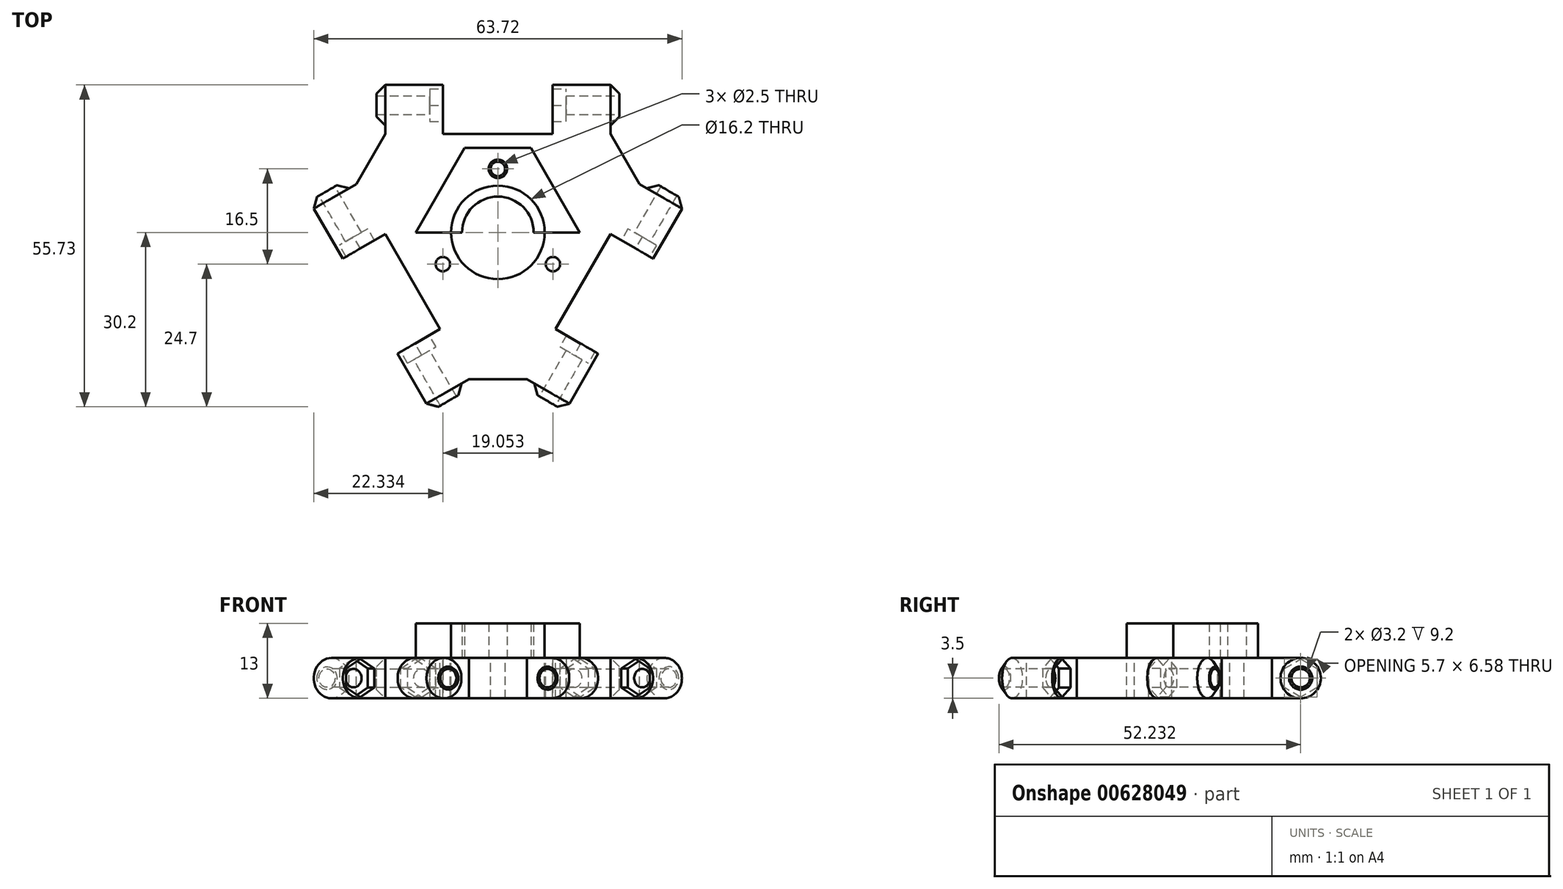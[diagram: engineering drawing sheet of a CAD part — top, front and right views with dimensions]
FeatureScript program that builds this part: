
annotation { "Feature Type Name" : "Feature", "Feature Type Description" : "" }
export const myFeature = defineFeature(function(context is Context, id is Id, definition is map)
    precondition{}
    {
        {
            assignVariable(context, id + "F0", {"name" : "side_inner_gap_width", "anyValue" : 19 * mm});
        }
        {
            assignVariable(context, id + "F1", {"name" : "side_arm_width", "anyValue" : 10 * mm});
        }
        {
            assignVariable(context, id + "F2", {"name" : "baseplate_thickness", "anyValue" : 7 * mm});
        }
        {
            assignVariable(context, id + "F3", {"name" : "rod_holder_indent", "anyValue" : 1.5 * mm});
        }
        {
            assignVariable(context, id + "F4", {"name" : "M3_nut_height", "anyValue" : 2.3 * mm});
        }
        {
            var Q0;
            Q0=qCreatedBy(makeId("Top.planeOp"),FACE);
            var sketch = newSketch(context, id + "F5", { "sketchPlane" : qUnion([Q0])});
            skCircle(sketch, "E0", {"center": v(0, 0) * mm, "radius": 8.1 * mm});
            skLineSegment(sketch, "E1", {"start": v(-9.5, 17.03) * mm, "end": v(9.5, 17.03) * mm});
            skLineSegment(sketch, "E2", {"start": v(9.5, 17.03) * mm, "end": v(9.5, 25.53) * mm});
            skLineSegment(sketch, "E3", {"start": v(9.5, 25.53) * mm, "end": v(19.5, 25.53) * mm});
            skLineSegment(sketch, "E4", {"start": v(19.5, 25.53) * mm, "end": v(19.5, 17.03) * mm});
            skLineSegment(sketch, "E5", {"start": v(19.5, 17.03) * mm, "end": v(24.5, 8.37) * mm});
            skLineSegment(sketch, "E6", {"start": v(24.5, 8.37) * mm, "end": v(31.86, 4.12) * mm});
            skLineSegment(sketch, "E7", {"start": v(31.86, 4.12) * mm, "end": v(26.86, -4.54) * mm});
            skLineSegment(sketch, "E8", {"start": v(-19.5, 17.03) * mm, "end": v(-19.5, 25.53) * mm});
            skLineSegment(sketch, "E9", {"start": v(-19.5, 25.53) * mm, "end": v(-9.5, 25.53) * mm});
            skLineSegment(sketch, "E10", {"start": v(-9.5, 25.53) * mm, "end": v(-9.5, 17.03) * mm});
            skLineSegment(sketch, "E11", {"start": v(26.86, -4.54) * mm, "end": v(19.5, -0.29) * mm});
            skLineSegment(sketch, "E12", {"start": v(19.5, -0.29) * mm, "end": v(10, -16.74) * mm});
            skLineSegment(sketch, "E13", {"start": v(10, -16.74) * mm, "end": v(17.36, -21) * mm});
            skLineSegment(sketch, "E14", {"start": v(17.36, -21) * mm, "end": v(12.36, -29.65) * mm});
            skLineSegment(sketch, "E15", {"start": v(12.36, -29.65) * mm, "end": v(5, -25.4) * mm});
            skLineSegment(sketch, "E16", {"start": v(5, -25.4) * mm, "end": v(-5, -25.4) * mm});
            skLineSegment(sketch, "E17", {"start": v(-5, -25.4) * mm, "end": v(-12.36, -29.65) * mm});
            skLineSegment(sketch, "E18", {"start": v(-12.36, -29.65) * mm, "end": v(-17.36, -21) * mm});
            skLineSegment(sketch, "E19", {"start": v(-17.36, -21) * mm, "end": v(-10, -16.74) * mm});
            skLineSegment(sketch, "E20", {"start": v(-19.5, 17.03) * mm, "end": v(-24.5, 8.37) * mm});
            skLineSegment(sketch, "E21", {"start": v(-24.5, 8.37) * mm, "end": v(-31.86, 4.12) * mm});
            skLineSegment(sketch, "E22", {"start": v(-31.86, 4.12) * mm, "end": v(-26.86, -4.54) * mm});
            skLineSegment(sketch, "E23", {"start": v(-26.86, -4.54) * mm, "end": v(-19.5, -0.29) * mm});
            skLineSegment(sketch, "E24", {"start": v(-19.5, -0.29) * mm, "end": v(-10, -16.74) * mm});
            skLineSegment(sketch, "E25", {"start": v(-9.5, 17.03) * mm, "end": v(0, 0) * mm, "construction": true});
            skLineSegment(sketch, "E26", {"start": v(19.5, -0.29) * mm, "end": v(0, 0) * mm, "construction": true});
            skLineSegment(sketch, "E27", {"start": v(-10, -16.74) * mm, "end": v(0, 0) * mm, "construction": true});
            skArc(sketch, "E28", {"start": v(-6.2, 0) * mm, "mid": v(0, 6.2) * mm, "end": v(6.2, 0) * mm});
            skLineSegment(sketch, "E29", {"start": v(6.2, 0) * mm, "end": v(14.2, 0) * mm});
            skLineSegment(sketch, "E30", {"start": v(14.2, 0) * mm, "end": v(5.75, 14.64) * mm});
            skLineSegment(sketch, "E31", {"start": v(5.75, 14.64) * mm, "end": v(-5.75, 14.64) * mm});
            skLineSegment(sketch, "E32", {"start": v(-5.75, 14.64) * mm, "end": v(-14.2, 0) * mm});
            skLineSegment(sketch, "E33", {"start": v(-14.2, 0) * mm, "end": v(-6.2, 0) * mm});
            skCircle(sketch, "E34", {"center": v(0, 11) * mm, "radius": 1.6 * mm});
            skCircle(sketch, "E35", {"center": v(0, 11) * mm, "radius": 1.25 * mm});
            skLineSegment(sketch, "E36", {"start": v(0, 11) * mm, "end": v(0, 0) * mm, "construction": true});
            skCircle(sketch, "E37.1.0", {"center": v(-9.53, -5.5) * mm, "radius": 1.25 * mm});
            skLineSegment(sketch, "E37.1.2", {"start": v(-9.53, -5.5) * mm, "end": v(0, 0) * mm, "construction": true});
            skCircle(sketch, "E37.2.0", {"center": v(9.53, -5.5) * mm, "radius": 1.25 * mm});
            skLineSegment(sketch, "E37.2.2", {"start": v(9.53, -5.5) * mm, "end": v(0, 0) * mm, "construction": true});
            skSolve(sketch);
        }
        {
            var Q0;
            Q0=makeQuery(id+"F5.imprint","IMPRINT",FACE,{"disambiguationData":[TD([[makeQuery(id+"F5.imprint","IMPRINT",EDGE,{"derivedFrom":sQuery(id+"F5.wireOp",EDGE,"E0")}),-1.0]])]});
            var Q1;
            Q1=makeQuery(id+"F5.imprint","IMPRINT",FACE,{"disambiguationData":[TD([[makeQuery(id+"F5.imprint","IMPRINT",EDGE,{"derivedFrom":sQuery(id+"F5.wireOp",EDGE,"E1")}),-1.0]])]});
            var Q2;
            Q2=makeQuery(id+"F5.imprint","IMPRINT",FACE,{"disambiguationData":[TD([[makeQuery(id+"F5.imprint","IMPRINT",EDGE,{"derivedFrom":sQuery(id+"F5.wireOp",EDGE,"E34")}),1.0]])]});
            var Q3;
            Q3=makeQuery(id+"F5.imprint","IMPRINT",FACE,{"disambiguationData":[TD([[makeQuery(id+"F5.imprint","IMPRINT",EDGE,{"derivedFrom":sQuery(id+"F5.wireOp",EDGE,"gB12h6lw-a8Tq-MIft-bfN1-dJZgKXMW2Zgf")}),-1.0]])]});
            extrude(context, id + "F6", {"entities" : qUnion([Q0, Q1, Q2, Q3]), "oppositeDirection" : true, "depth" : getVariable(context, 'baseplate_thickness'), "offsetDistance" : 25 * mm});
        }
        {
            var Q0;
            {var subQ0=sQuery(id+"F5.wireOp",EDGE,"E30");Q0=makeQuery(id+"F5.imprint","IMPRINT",FACE,{"disambiguationData":[TD([[makeQuery(id+"F5.imprint","IMPRINT",EDGE,{"derivedFrom":subQ0}),1.0]])]});}
            var Q1;
            {var subQ5=sQuery(id+"F5.wireOp",EDGE,"E28");Q1=makeQuery(id+"F5.imprint","IMPRINT",FACE,{"disambiguationData":[TD([[makeQuery(id+"F5.imprint","IMPRINT",EDGE,{"derivedFrom":subQ5}),1.0]])]});}
            extrude(context, id + "F7", {"entities" : qUnion([Q0, Q1]), "depth" : 6 * mm, "offsetDistance" : 25 * mm});
        }
        {
            var Q0;
            Q0=makeQuery(id+"F6.opExtrude","CAP_EDGE",EDGE,{"disambiguationData":[OSD([sQuery(id+"F5.wireOp",EDGE,"E14")])],"isStart":false});
            var Q1;
            Q1=makeQuery(id+"F6.opExtrude","CAP_EDGE",EDGE,{"disambiguationData":[OSD([sQuery(id+"F5.wireOp",EDGE,"E7")])],"isStart":false});
            var Q2;
            Q2=makeQuery(id+"F6.opExtrude","CAP_EDGE",EDGE,{"disambiguationData":[OSD([sQuery(id+"F5.wireOp",EDGE,"E14")])],"isStart":true});
            var Q3;
            Q3=makeQuery(id+"F6.opExtrude","CAP_EDGE",EDGE,{"disambiguationData":[OSD([sQuery(id+"F5.wireOp",EDGE,"E7")])],"isStart":true});
            var Q4;
            Q4=makeQuery(id+"F6.opExtrude","CAP_EDGE",EDGE,{"disambiguationData":[OSD([sQuery(id+"F5.wireOp",EDGE,"E18")])],"isStart":false});
            var Q5;
            Q5=makeQuery(id+"F6.opExtrude","CAP_EDGE",EDGE,{"disambiguationData":[OSD([sQuery(id+"F5.wireOp",EDGE,"E18")])],"isStart":true});
            var Q6;
            Q6=makeQuery(id+"F6.opExtrude","CAP_EDGE",EDGE,{"disambiguationData":[OSD([sQuery(id+"F5.wireOp",EDGE,"E22")])],"isStart":true});
            var Q7;
            Q7=makeQuery(id+"F6.opExtrude","CAP_EDGE",EDGE,{"disambiguationData":[OSD([sQuery(id+"F5.wireOp",EDGE,"E22")])],"isStart":false});
            var Q8;
            Q8=makeQuery(id+"F6.opExtrude","CAP_EDGE",EDGE,{"disambiguationData":[OSD([sQuery(id+"F5.wireOp",EDGE,"E3")])],"isStart":false});
            var Q9;
            Q9=makeQuery(id+"F6.opExtrude","CAP_EDGE",EDGE,{"disambiguationData":[OSD([sQuery(id+"F5.wireOp",EDGE,"E9")])],"isStart":false});
            var Q10;
            Q10=makeQuery(id+"F6.opExtrude","CAP_EDGE",EDGE,{"disambiguationData":[OSD([sQuery(id+"F5.wireOp",EDGE,"E3")])],"isStart":true});
            var Q11;
            Q11=makeQuery(id+"F6.opExtrude","CAP_EDGE",EDGE,{"disambiguationData":[OSD([sQuery(id+"F5.wireOp",EDGE,"E9")])],"isStart":true});
            fillet(context, id + "F8", {"entities" : qUnion([Q0, Q1, Q2, Q3, Q4, Q5, Q6, Q7, Q8, Q9, Q10, Q11]), "radius" : getVariable(context, 'baseplate_thickness') / 2, "tangentPropagation" : true, "allowEdgeOverflow" : false});
        }
        {
            var Q0;
            Q0=makeQuery(id+"F6.opExtrude","SWEPT_FACE",FACE,{"disambiguationData":[OSD([sQuery(id+"F5.wireOp",EDGE,"E11")])]});
            var sketch = newSketch(context, id + "F9", { "sketchPlane" : qUnion([Q0])});
            skCircle(sketch, "E38", {"center": v(22.03, -3.5) * mm, "radius": 3.5 * mm});
            skCircle(sketch, "E39.cCircle", {"center": v(22.03, -3.5) * mm, "radius": 3.3 * mm, "construction": true});
            skLineSegment(sketch, "E39.0", {"start": v(22.03, -0.2) * mm, "end": v(24.88, -1.85) * mm});
            skLineSegment(sketch, "E39.1", {"start": v(24.88, -1.85) * mm, "end": v(24.88, -5.15) * mm});
            skLineSegment(sketch, "E39.2", {"start": v(24.88, -5.15) * mm, "end": v(22.03, -6.8) * mm});
            skLineSegment(sketch, "E39.3", {"start": v(22.03, -6.8) * mm, "end": v(19.18, -5.15) * mm});
            skLineSegment(sketch, "E39.4", {"start": v(19.18, -5.15) * mm, "end": v(19.18, -1.85) * mm});
            skLineSegment(sketch, "E39.5", {"start": v(19.18, -1.85) * mm, "end": v(22.03, -0.2) * mm});
            skCircle(sketch, "E40", {"center": v(22.03, -3.5) * mm, "radius": 1.6 * mm});
            skSolve(sketch);
        }
        {
            var Q0;
            {var subQ0=sQuery(id+"F9.wireOp",EDGE,"E38");var subQ1=sQuery(id+"F5.wireOp",EDGE,"E11");var subQ4=makeQuery(id+"F9.imprint","INTERSECT",VERTEX,{"derivedFrom":[makeQuery(id+"F6.opExtrude","CAP_EDGE",EDGE,{"disambiguationData":[OSD([subQ1])],"isStart":true}),subQ0]});Q0=makeQuery(id+"F9.imprint","IMPRINT",FACE,{"disambiguationData":[TD([[makeQuery(id+"F9.imprint","IMPRINT",EDGE,{"disambiguationData":[TD([[subQ4,-1.0]])],"derivedFrom":subQ0}),1.0]])]});}
            var Q1;
            Q1=makeQuery(id+"F9.imprint","IMPRINT",FACE,{"disambiguationData":[TD([[makeQuery(id+"F9.imprint","IMPRINT",EDGE,{"derivedFrom":sQuery(id+"F9.wireOp",EDGE,"E39.0")}),-1.0]])]});
            extrude(context, id + "F10", {"entities" : qUnion([Q0, Q1]), "operationType" : NewBodyOperationType.ADD, "oppositeDirection" : true, "depth" : getVariable(context, 'side_arm_width') + getVariable(context, 'rod_holder_indent'), "offsetDistance" : 25 * mm, "hasSecondDirection" : true, "secondDirectionOppositeDirection" : false, "secondDirectionDepth" : getVariable(context, 'side_inner_gap_width') + getVariable(context, 'side_arm_width') + getVariable(context, 'rod_holder_indent')});
        }
        {
            var Q0;
            Q0=makeQuery(id+"F9.imprint","IMPRINT",FACE,{"disambiguationData":[TD([[makeQuery(id+"F9.imprint","IMPRINT",EDGE,{"derivedFrom":sQuery(id+"F9.wireOp",EDGE,"E39.0")}),1.0]])]});
            var Q1;
            Q1=makeQuery(id+"F9.imprint","IMPRINT",FACE,{"disambiguationData":[TD([[makeQuery(id+"F9.imprint","IMPRINT",EDGE,{"derivedFrom":sQuery(id+"F9.wireOp",EDGE,"E39.0")}),-1.0]])]});
            extrude(context, id + "F11", {"entities" : qUnion([Q0, Q1]), "operationType" : NewBodyOperationType.REMOVE, "depth" : getVariable(context, 'side_inner_gap_width'), "offsetDistance" : 25 * mm});
        }
        {
            var Q0;
            Q0=makeQuery(id+"F9.imprint","IMPRINT",FACE,{"disambiguationData":[TD([[makeQuery(id+"F9.imprint","IMPRINT",EDGE,{"derivedFrom":sQuery(id+"F9.wireOp",EDGE,"E39.0")}),-1.0]])]});
            extrude(context, id + "F12", {"entities" : qUnion([Q0]), "operationType" : NewBodyOperationType.REMOVE, "oppositeDirection" : true, "depth" : getVariable(context, 'M3_nut_height'), "offsetDistance" : 25 * mm, "hasSecondDirection" : true, "secondDirectionOppositeDirection" : false, "secondDirectionDepth" : getVariable(context, 'side_inner_gap_width') + getVariable(context, 'M3_nut_height')});
        }
        {
            var Q0;
            Q0=makeQuery(id+"F9.imprint","IMPRINT",FACE,{"disambiguationData":[TD([[makeQuery(id+"F9.imprint","IMPRINT",EDGE,{"derivedFrom":sQuery(id+"F9.wireOp",EDGE,"E40")}),1.0]])]});
            extrude(context, id + "F13", {"entities" : qUnion([Q0]), "operationType" : NewBodyOperationType.REMOVE, "oppositeDirection" : true, "depth" : getVariable(context, 'side_arm_width'), "offsetDistance" : 25 * mm, "hasSecondDirection" : true, "secondDirectionOppositeDirection" : false, "secondDirectionDepth" : getVariable(context, 'side_inner_gap_width') + getVariable(context, 'side_arm_width')});
        }
        {
            var Q0;
            Q0=makeQuery(id+"F6.opExtrude","SWEPT_FACE",FACE,{"disambiguationData":[OSD([sQuery(id+"F5.wireOp",EDGE,"E19")])]});
            var sketch = newSketch(context, id + "F14", { "sketchPlane" : qUnion([Q0])});
            skCircle(sketch, "E41", {"center": v(22.03, -3.5) * mm, "radius": 3.5 * mm});
            skCircle(sketch, "E42.cCircle", {"center": v(22.03, -3.5) * mm, "radius": 3.3 * mm, "construction": true});
            skLineSegment(sketch, "E42.0", {"start": v(22.03, -0.2) * mm, "end": v(24.88, -1.85) * mm});
            skLineSegment(sketch, "E42.1", {"start": v(24.88, -1.85) * mm, "end": v(24.88, -5.15) * mm});
            skLineSegment(sketch, "E42.2", {"start": v(24.88, -5.15) * mm, "end": v(22.03, -6.8) * mm});
            skLineSegment(sketch, "E42.3", {"start": v(22.03, -6.8) * mm, "end": v(19.18, -5.15) * mm});
            skLineSegment(sketch, "E42.4", {"start": v(19.18, -5.15) * mm, "end": v(19.18, -1.85) * mm});
            skLineSegment(sketch, "E42.5", {"start": v(19.18, -1.85) * mm, "end": v(22.03, -0.2) * mm});
            skCircle(sketch, "E43", {"center": v(22.03, -3.5) * mm, "radius": 1.6 * mm});
            skSolve(sketch);
        }
        {
            var Q0;
            {var subQ0=sQuery(id+"F14.wireOp",EDGE,"E41");var subQ1=sQuery(id+"F5.wireOp",EDGE,"E19");var subQ2=makeQuery(id+"F14.imprint","INTERSECT",VERTEX,{"derivedFrom":[makeQuery(id+"F6.opExtrude","CAP_EDGE",EDGE,{"disambiguationData":[OSD([subQ1])],"isStart":true}),subQ0]});Q0=makeQuery(id+"F14.imprint","IMPRINT",FACE,{"disambiguationData":[TD([[makeQuery(id+"F14.imprint","IMPRINT",EDGE,{"disambiguationData":[TD([[subQ2,1.0]])],"derivedFrom":subQ0}),1.0]])]});}
            var Q1;
            Q1=makeQuery(id+"F14.imprint","IMPRINT",FACE,{"disambiguationData":[TD([[makeQuery(id+"F14.imprint","IMPRINT",EDGE,{"derivedFrom":sQuery(id+"F14.wireOp",EDGE,"E42.0")}),-1.0]])]});
            extrude(context, id + "F15", {"entities" : qUnion([Q0, Q1]), "operationType" : NewBodyOperationType.ADD, "oppositeDirection" : true, "depth" : getVariable(context, 'side_arm_width') + getVariable(context, 'rod_holder_indent'), "offsetDistance" : 25 * mm, "hasSecondDirection" : true, "secondDirectionOppositeDirection" : false, "secondDirectionDepth" : getVariable(context, 'side_inner_gap_width') + getVariable(context, 'side_arm_width') + getVariable(context, 'rod_holder_indent')});
        }
        {
            var Q0;
            Q0=makeQuery(id+"F14.imprint","IMPRINT",FACE,{"disambiguationData":[TD([[makeQuery(id+"F14.imprint","IMPRINT",EDGE,{"derivedFrom":sQuery(id+"F14.wireOp",EDGE,"E42.0")}),1.0]])]});
            var Q1;
            Q1=makeQuery(id+"F14.imprint","IMPRINT",FACE,{"disambiguationData":[TD([[makeQuery(id+"F14.imprint","IMPRINT",EDGE,{"derivedFrom":sQuery(id+"F14.wireOp",EDGE,"E42.0")}),-1.0]])]});
            extrude(context, id + "F16", {"entities" : qUnion([Q0, Q1]), "operationType" : NewBodyOperationType.REMOVE, "depth" : getVariable(context, 'side_inner_gap_width'), "offsetDistance" : 25 * mm});
        }
        {
            var Q0;
            Q0=makeQuery(id+"F14.imprint","IMPRINT",FACE,{"disambiguationData":[TD([[makeQuery(id+"F14.imprint","IMPRINT",EDGE,{"derivedFrom":sQuery(id+"F14.wireOp",EDGE,"E42.0")}),-1.0]])]});
            extrude(context, id + "F17", {"entities" : qUnion([Q0]), "operationType" : NewBodyOperationType.REMOVE, "oppositeDirection" : true, "depth" : getVariable(context, 'M3_nut_height'), "offsetDistance" : 25 * mm, "hasSecondDirection" : true, "secondDirectionOppositeDirection" : false, "secondDirectionDepth" : getVariable(context, 'side_inner_gap_width') + getVariable(context, 'M3_nut_height')});
        }
        {
            var Q0;
            Q0=makeQuery(id+"F14.imprint","IMPRINT",FACE,{"disambiguationData":[TD([[makeQuery(id+"F14.imprint","IMPRINT",EDGE,{"derivedFrom":sQuery(id+"F14.wireOp",EDGE,"E43")}),1.0]])]});
            extrude(context, id + "F18", {"entities" : qUnion([Q0]), "operationType" : NewBodyOperationType.REMOVE, "oppositeDirection" : true, "depth" : getVariable(context, 'side_arm_width'), "offsetDistance" : 25 * mm, "hasSecondDirection" : true, "secondDirectionOppositeDirection" : false, "secondDirectionDepth" : getVariable(context, 'side_inner_gap_width') + getVariable(context, 'side_arm_width')});
        }
        {
            var Q0;
            Q0=makeQuery(id+"F6.opExtrude","SWEPT_FACE",FACE,{"disambiguationData":[OSD([sQuery(id+"F5.wireOp",EDGE,"E10")])]});
            var sketch = newSketch(context, id + "F19", { "sketchPlane" : qUnion([Q0])});
            skCircle(sketch, "E44", {"center": v(22.03, -3.5) * mm, "radius": 3.5 * mm});
            skCircle(sketch, "E45.cCircle", {"center": v(22.03, -3.5) * mm, "radius": 3.3 * mm, "construction": true});
            skLineSegment(sketch, "E45.0", {"start": v(22.03, -0.2) * mm, "end": v(24.88, -1.85) * mm});
            skLineSegment(sketch, "E45.1", {"start": v(24.88, -1.85) * mm, "end": v(24.88, -5.15) * mm});
            skLineSegment(sketch, "E45.2", {"start": v(24.88, -5.15) * mm, "end": v(22.03, -6.8) * mm});
            skLineSegment(sketch, "E45.3", {"start": v(22.03, -6.8) * mm, "end": v(19.18, -5.15) * mm});
            skLineSegment(sketch, "E45.4", {"start": v(19.18, -5.15) * mm, "end": v(19.18, -1.85) * mm});
            skLineSegment(sketch, "E45.5", {"start": v(19.18, -1.85) * mm, "end": v(22.03, -0.2) * mm});
            skCircle(sketch, "E46", {"center": v(22.03, -3.5) * mm, "radius": 1.6 * mm});
            skSolve(sketch);
        }
        {
            var Q0;
            {var subQ0=sQuery(id+"F19.wireOp",EDGE,"E44");var subQ1=sQuery(id+"F5.wireOp",EDGE,"E10");var subQ2=makeQuery(id+"F19.imprint","INTERSECT",VERTEX,{"derivedFrom":[makeQuery(id+"F6.opExtrude","CAP_EDGE",EDGE,{"disambiguationData":[OSD([subQ1])],"isStart":true}),subQ0]});Q0=makeQuery(id+"F19.imprint","IMPRINT",FACE,{"disambiguationData":[TD([[makeQuery(id+"F19.imprint","IMPRINT",EDGE,{"disambiguationData":[TD([[subQ2,1.0]])],"derivedFrom":subQ0}),1.0]])]});}
            var Q1;
            Q1=makeQuery(id+"F19.imprint","IMPRINT",FACE,{"disambiguationData":[TD([[makeQuery(id+"F19.imprint","IMPRINT",EDGE,{"derivedFrom":sQuery(id+"F19.wireOp",EDGE,"E45.0")}),-1.0]])]});
            extrude(context, id + "F20", {"entities" : qUnion([Q0, Q1]), "operationType" : NewBodyOperationType.ADD, "oppositeDirection" : true, "depth" : getVariable(context, 'side_arm_width') + getVariable(context, 'rod_holder_indent'), "offsetDistance" : 25 * mm, "hasSecondDirection" : true, "secondDirectionOppositeDirection" : false, "secondDirectionDepth" : getVariable(context, 'side_inner_gap_width') + getVariable(context, 'side_arm_width') + getVariable(context, 'rod_holder_indent')});
        }
        {
            var Q0;
            Q0=makeQuery(id+"F19.imprint","IMPRINT",FACE,{"disambiguationData":[TD([[makeQuery(id+"F19.imprint","IMPRINT",EDGE,{"derivedFrom":sQuery(id+"F19.wireOp",EDGE,"E45.0")}),1.0]])]});
            var Q1;
            Q1=makeQuery(id+"F19.imprint","IMPRINT",FACE,{"disambiguationData":[TD([[makeQuery(id+"F19.imprint","IMPRINT",EDGE,{"derivedFrom":sQuery(id+"F19.wireOp",EDGE,"E45.0")}),-1.0]])]});
            extrude(context, id + "F21", {"entities" : qUnion([Q0, Q1]), "operationType" : NewBodyOperationType.REMOVE, "depth" : getVariable(context, 'side_inner_gap_width'), "offsetDistance" : 25 * mm});
        }
        {
            var Q0;
            Q0=makeQuery(id+"F19.imprint","IMPRINT",FACE,{"disambiguationData":[TD([[makeQuery(id+"F19.imprint","IMPRINT",EDGE,{"derivedFrom":sQuery(id+"F19.wireOp",EDGE,"E45.0")}),-1.0]])]});
            extrude(context, id + "F22", {"entities" : qUnion([Q0]), "operationType" : NewBodyOperationType.REMOVE, "oppositeDirection" : true, "depth" : getVariable(context, 'M3_nut_height'), "offsetDistance" : 25 * mm, "hasSecondDirection" : true, "secondDirectionOppositeDirection" : false, "secondDirectionDepth" : getVariable(context, 'side_inner_gap_width') + getVariable(context, 'M3_nut_height')});
        }
        {
            var Q0;
            Q0=makeQuery(id+"F19.imprint","IMPRINT",FACE,{"disambiguationData":[TD([[makeQuery(id+"F19.imprint","IMPRINT",EDGE,{"derivedFrom":sQuery(id+"F19.wireOp",EDGE,"E46")}),1.0]])]});
            extrude(context, id + "F23", {"entities" : qUnion([Q0]), "operationType" : NewBodyOperationType.REMOVE, "oppositeDirection" : true, "depth" : getVariable(context, 'side_arm_width'), "offsetDistance" : 25 * mm, "hasSecondDirection" : true, "secondDirectionOppositeDirection" : false, "secondDirectionDepth" : getVariable(context, 'side_inner_gap_width') + getVariable(context, 'side_arm_width')});
        }
        {
            var Q0;
            Q0=makeQuery(id+"F10.opExtrude","CAP_EDGE",EDGE,{"disambiguationData":[OSD([sQuery(id+"F9.wireOp",EDGE,"E38")])],"isStart":false});
            var Q1;
            Q1=makeQuery(id+"F10.opExtrude","CAP_EDGE",EDGE,{"disambiguationData":[OSD([sQuery(id+"F9.wireOp",EDGE,"E38")])],"isStart":true});
            var Q2;
            Q2=makeQuery(id+"F15.opExtrude","CAP_EDGE",EDGE,{"disambiguationData":[OSD([sQuery(id+"F14.wireOp",EDGE,"E41")])],"isStart":false});
            var Q3;
            Q3=makeQuery(id+"F15.opExtrude","CAP_EDGE",EDGE,{"disambiguationData":[OSD([sQuery(id+"F14.wireOp",EDGE,"E41")])],"isStart":true});
            var Q4;
            Q4=makeQuery(id+"F20.opExtrude","CAP_EDGE",EDGE,{"disambiguationData":[OSD([sQuery(id+"F19.wireOp",EDGE,"E44")])],"isStart":true});
            var Q5;
            Q5=makeQuery(id+"F20.opExtrude","CAP_EDGE",EDGE,{"disambiguationData":[OSD([sQuery(id+"F19.wireOp",EDGE,"E44")])],"isStart":false});
            chamfer(context, id + "F24", {"entities" : qUnion([Q0, Q1, Q2, Q3, Q4, Q5]), "chamferType" : ChamferType.TWO_OFFSETS, "width1" : 1.5 * mm, "oppositeDirection" : false, "width2" : 1.5 * mm, "tangentPropagation" : true});
        }
    });
